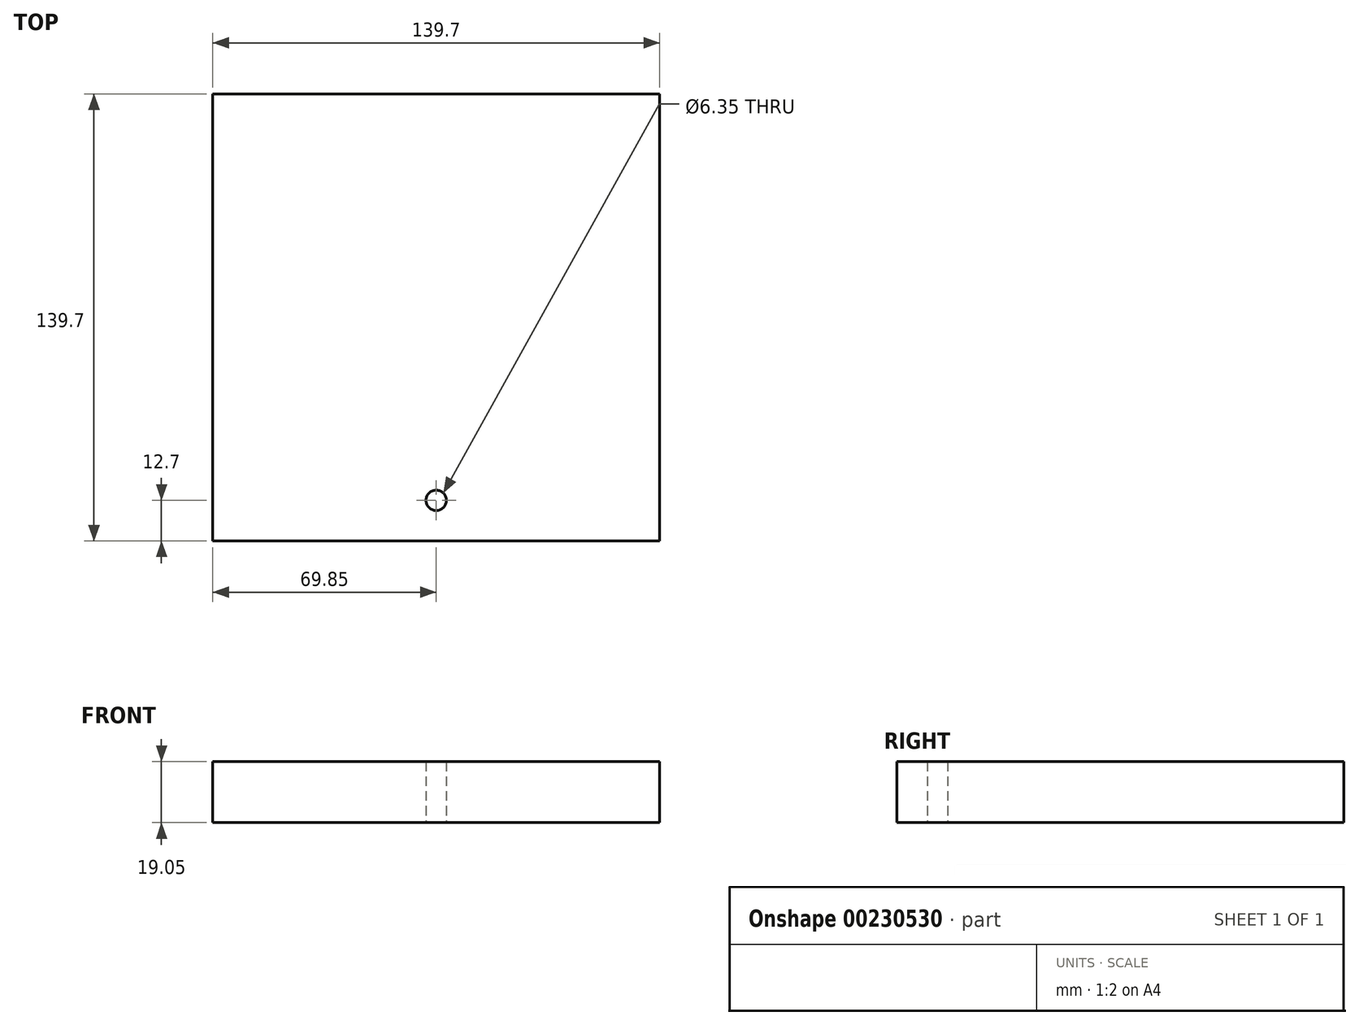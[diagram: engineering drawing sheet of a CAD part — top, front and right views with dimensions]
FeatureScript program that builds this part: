
annotation { "Feature Type Name" : "Feature", "Feature Type Description" : "" }
export const myFeature = defineFeature(function(context is Context, id is Id, definition is map)
    precondition{}
    {
        {
            var Q0;
            Q0=qCreatedBy(makeId("Top.planeOp"),FACE);
            var sketch = newSketch(context, id + "F0", { "sketchPlane" : qUnion([Q0])});
            skLineSegment(sketch, "E0.bottom", {"start": v(-69.85, -69.85) * mm, "end": v(69.85, -69.85) * mm});
            skLineSegment(sketch, "E0.top", {"start": v(-69.85, 69.85) * mm, "end": v(69.85, 69.85) * mm});
            skLineSegment(sketch, "E0.left", {"start": v(-69.85, -69.85) * mm, "end": v(-69.85, 69.85) * mm});
            skLineSegment(sketch, "E0.right", {"start": v(69.85, -69.85) * mm, "end": v(69.85, 69.85) * mm});
            skPoint(sketch, "E0.middle", {"position": v(0, 0) * mm});
            skLineSegment(sketch, "E1", {"start": v(0, -69.85) * mm, "end": v(0, -57.15) * mm});
            skPoint(sketch, "E1.endSnap0", {"position": v(0, -69.85) * mm});
            skCircle(sketch, "E2", {"center": v(0, -57.15) * mm, "radius": 3.18 * mm});
            skSolve(sketch);
        }
        {
            var Q0;
            Q0=makeQuery(id+"F0.imprint","IMPRINT",FACE,{"disambiguationData":[TD([[makeQuery(id+"F0.imprint","IMPRINT",EDGE,{"derivedFrom":sQuery(id+"F0.wireOp",EDGE,"E0.top")}),-1.0]])]});
            extrude(context, id + "F1", {"entities" : qUnion([Q0]), "depth" : 19.05 * mm});
        }
    });
